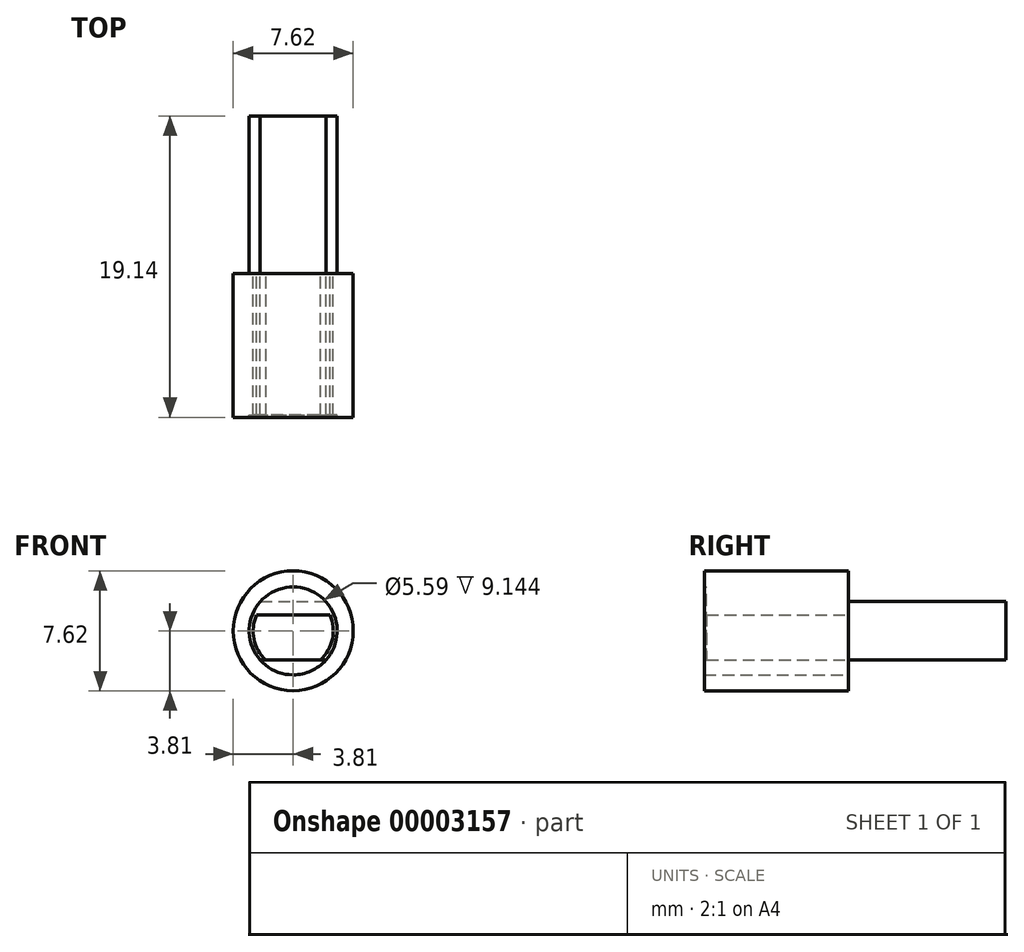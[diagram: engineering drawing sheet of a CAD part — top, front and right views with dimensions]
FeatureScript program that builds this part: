
annotation { "Feature Type Name" : "Feature", "Feature Type Description" : "" }
export const myFeature = defineFeature(function(context is Context, id is Id, definition is map)
    precondition{}
    {
        {
            var Q0;
            Q0=qCreatedBy(makeId("Front.planeOp"),FACE);
            var sketch = newSketch(context, id + "F0", { "sketchPlane" : qUnion([Q0])});
            skArc(sketch, "E0", {"start": v(-2.33, 1.02) * mm, "mid": v(0, -2.54) * mm, "end": v(2.33, 1.02) * mm});
            skLineSegment(sketch, "E1", {"start": v(-2.33, 1.02) * mm, "end": v(2.33, 1.02) * mm});
            skCircle(sketch, "E2", {"center": v(0, 0) * mm, "radius": 2.8 * mm});
            skLineSegment(sketch, "E3", {"start": v(-2.1, -1.85) * mm, "end": v(2.1, -1.85) * mm});
            skLineSegment(sketch, "E4", {"start": v(-2.1, 1.85) * mm, "end": v(2.1, 1.85) * mm});
            skCircle(sketch, "E5", {"center": v(0, 0) * mm, "radius": 3.81 * mm});
            skSolve(sketch);
        }
        {
            var Q0;
            {var subQ0=sQuery(id+"F0.wireOp",EDGE,"E4");Q0=makeQuery(id+"F0.imprint","IMPRINT",FACE,{"disambiguationData":[TD([[makeQuery(id+"F0.imprint","IMPRINT",EDGE,{"derivedFrom":subQ0}),1.0]])]});}
            var Q1;
            {var subQ8=sQuery(id+"F0.wireOp",EDGE,"E1");Q1=makeQuery(id+"F0.imprint","IMPRINT",FACE,{"disambiguationData":[TD([[makeQuery(id+"F0.imprint","IMPRINT",EDGE,{"derivedFrom":subQ8}),1.0]])]});}
            var Q2;
            {var subQ0=sQuery(id+"F0.wireOp",EDGE,"E3");var subQ1=sQuery(id+"F0.wireOp",EDGE,"E0");var subQ5=makeQuery(id+"F0.imprint","INTERSECT",VERTEX,{"disambiguationData":[OD(0.0)],"derivedFrom":[subQ1,subQ0]});Q2=makeQuery(id+"F0.imprint","IMPRINT",FACE,{"disambiguationData":[TD([[makeQuery(id+"F0.imprint","IMPRINT",EDGE,{"disambiguationData":[TD([[subQ5,-1.0]])],"derivedFrom":subQ1}),-1.0]])]});}
            extrude(context, id + "F1", {"entities" : qUnion([Q0, Q1, Q2]), "depth" : 9 * mm});
        }
        {
            var Q0;
            {var subQ4=sQuery(id+"F0.wireOp",EDGE,"E1");Q0=makeQuery(id+"F0.imprint","IMPRINT",FACE,{"disambiguationData":[TD([[makeQuery(id+"F0.imprint","IMPRINT",EDGE,{"derivedFrom":subQ4}),-1.0]])]});}
            var Q1;
            {var subQ8=sQuery(id+"F0.wireOp",EDGE,"E1");Q1=makeQuery(id+"F0.imprint","IMPRINT",FACE,{"disambiguationData":[TD([[makeQuery(id+"F0.imprint","IMPRINT",EDGE,{"derivedFrom":subQ8}),1.0]])]});}
            extrude(context, id + "F2", {"entities" : qUnion([Q0, Q1]), "operationType" : NewBodyOperationType.ADD, "oppositeDirection" : true, "depth" : 10 * mm});
        }
        {
            var Q0;
            Q0=makeQuery(id+"F0.imprint","IMPRINT",FACE,{"disambiguationData":[TD([[makeQuery(id+"F0.imprint","IMPRINT",EDGE,{"derivedFrom":sQuery(id+"F0.wireOp",EDGE,"E5")}),1.0]])]});
            extrude(context, id + "F3", {"entities" : qUnion([Q0]), "operationType" : NewBodyOperationType.ADD, "depth" : 9.14 * mm});
        }
    });
